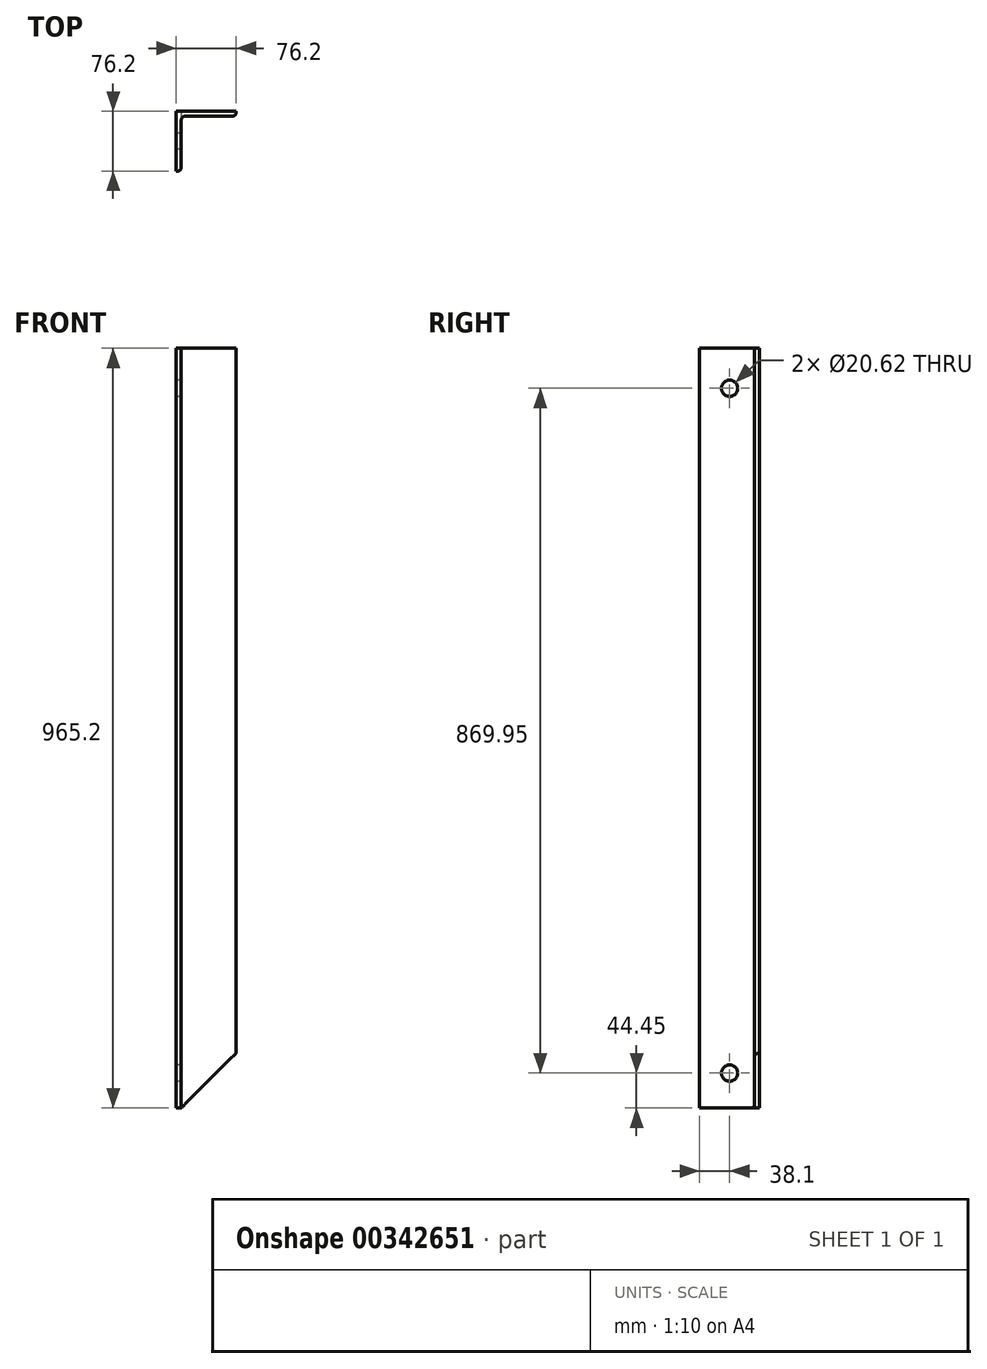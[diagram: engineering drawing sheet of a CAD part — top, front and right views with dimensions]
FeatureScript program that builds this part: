
annotation { "Feature Type Name" : "Feature", "Feature Type Description" : "" }
export const myFeature = defineFeature(function(context is Context, id is Id, definition is map)
    precondition{}
    {
        {
            var Q0;
            Q0=qCreatedBy(makeId("Top.planeOp"),FACE);
            var sketch = newSketch(context, id + "F0", { "sketchPlane" : qUnion([Q0])});
            skLineSegment(sketch, "E0", {"start": v(0, 0) * mm, "end": v(0, 76.2) * mm});
            skLineSegment(sketch, "E1", {"start": v(0, 76.2) * mm, "end": v(76.2, 76.2) * mm});
            skLineSegment(sketch, "E2", {"start": v(76.2, 76.2) * mm, "end": v(76.2, 69.85) * mm});
            skLineSegment(sketch, "E3", {"start": v(76.2, 69.85) * mm, "end": v(6.35, 69.85) * mm});
            skLineSegment(sketch, "E4", {"start": v(6.35, 69.85) * mm, "end": v(6.35, 0) * mm});
            skLineSegment(sketch, "E5", {"start": v(6.35, 0) * mm, "end": v(0, 0) * mm});
            skSolve(sketch);
        }
        {
            var Q0;
            Q0 = qSketchRegion(id + "F0", true);
            extrude(context, id + "F1", {"entities" : qUnion([Q0]), "endBound" : BoundingType.SYMMETRIC, "depth" : 965.2 * mm});
        }
        {
            var Q0;
            Q0=qCreatedBy(makeId("Front.planeOp"),FACE);
            var sketch = newSketch(context, id + "F2", { "sketchPlane" : qUnion([Q0])});
            skPoint(sketch, "E6.0", {"position": v(6.35, -482.6) * mm});
            skLineSegment(sketch, "E7", {"start": v(6.35, -482.6) * mm, "end": v(84.52, -404.43) * mm});
            skLineSegment(sketch, "E8", {"start": v(84.52, -404.43) * mm, "end": v(84.52, -482.6) * mm});
            skLineSegment(sketch, "E9", {"start": v(84.52, -482.6) * mm, "end": v(6.35, -482.6) * mm});
            skSolve(sketch);
        }
        {
            var Q0;
            Q0 = qSketchRegion(id + "F2", true);
            extrude(context, id + "F3", {"entities" : qUnion([Q0]), "operationType" : NewBodyOperationType.REMOVE, "endBound" : BoundingType.THROUGH_ALL, "oppositeDirection" : true, "depth" : 25.4 * mm});
        }
        {
            var Q0;
            Q0=qCreatedBy(makeId("Right.planeOp"),FACE);
            var sketch = newSketch(context, id + "F4", { "sketchPlane" : qUnion([Q0])});
            skCircle(sketch, "E10", {"center": v(38.1, -438.15) * mm, "radius": 10.31 * mm});
            skCircle(sketch, "E11", {"center": v(38.1, 431.8) * mm, "radius": 10.31 * mm});
            skSolve(sketch);
        }
        {
            var Q0;
            Q0 = qSketchRegion(id + "F4", true);
            extrude(context, id + "F5", {"entities" : qUnion([Q0]), "operationType" : NewBodyOperationType.REMOVE, "endBound" : BoundingType.THROUGH_ALL, "depth" : 25.4 * mm});
        }
        {
            var Q0;
            Q0=makeQuery(id+"F1.opExtrude","SWEPT_EDGE",EDGE,{"disambiguationData":[OSD([sQuery(id+"F0.wireOp",EDGE,"E3"),sQuery(id+"F0.wireOp",EDGE,"E4")])]});
            var Q1;
            Q1=makeQuery(id+"F1.opExtrude","SWEPT_EDGE",EDGE,{"disambiguationData":[OSD([sQuery(id+"F0.wireOp",EDGE,"E2"),sQuery(id+"F0.wireOp",EDGE,"E3")])]});
            var Q2;
            Q2=makeQuery(id+"F1.opExtrude","SWEPT_EDGE",EDGE,{"disambiguationData":[OSD([sQuery(id+"F0.wireOp",EDGE,"E4"),sQuery(id+"F0.wireOp",EDGE,"E5")])]});
            fillet(context, id + "F6", {"entities" : qUnion([Q0, Q1, Q2]), "radius" : 5.08 * mm, "tangentPropagation" : true, "allowEdgeOverflow" : false});
        }
    });
